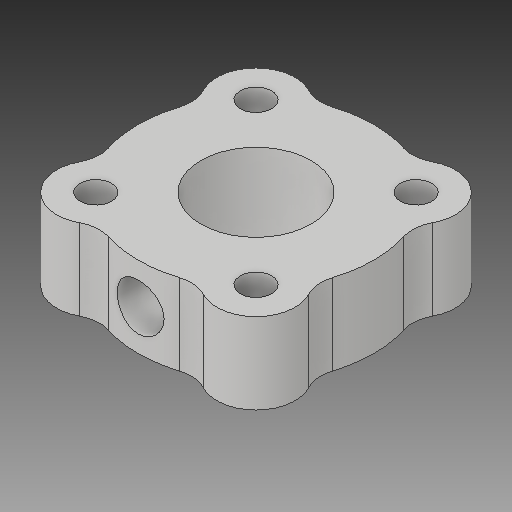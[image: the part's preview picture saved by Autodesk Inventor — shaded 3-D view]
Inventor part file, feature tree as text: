
AUTODESK INVENTOR PART (.ipt)
format: ipt  version: 2017 (Build 210142000, 142)  size: 150,528 bytes
history: native  units: in
note: dims shown in document units (in); Inventor stores cm internally (conversion verified against a paired STEP export)
features: fillet x1
ambient origin geometry x8: Origin, YZ Plane, XZ Plane, XY Plane, X Axis, Y Axis, Z Axis, Center Point
bodies: Solid1 (feature_tree)
feature tree (1):
  fillet  "Fillet1"  [1 undecoded]
note: 1 required parameter value undecoded (feature->parameter linkage not recoverable at this tier; creation-order binding heuristic only, values carry confidence <= 0.55)
